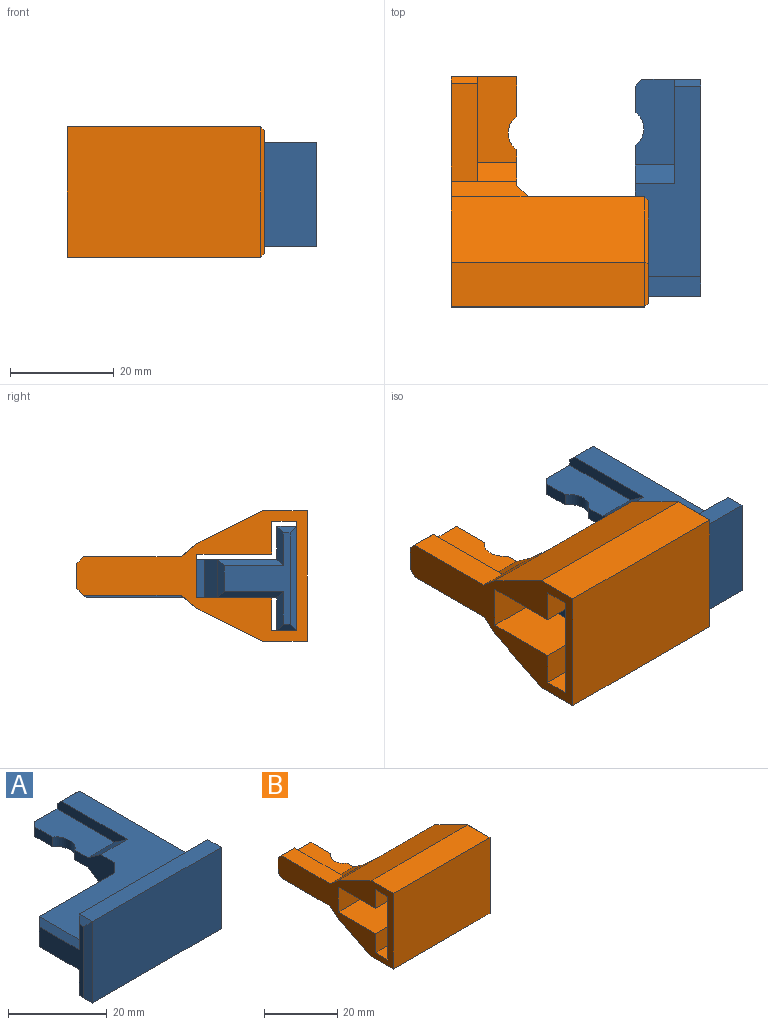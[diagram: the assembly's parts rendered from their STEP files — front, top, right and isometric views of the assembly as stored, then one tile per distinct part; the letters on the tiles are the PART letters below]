
ASSEMBLY  parts=2 mates=2
PART A: 32 faces, bbox 38.1x41.9x20.2 mm
  f0: plane 16.51x7.62mm, normal (0,0,1), area 117.4mm2, adj f2,f4,f6,f7,f8,f26,f29
  f1: plane 16.51x7.62mm, normal (0,0,-1), area 117.4mm2, adj f3,f4,f6,f7,f8,f26,f28
  f2: plane 7.62x3.63mm, normal (0,0.57,0.82), area 33.7mm2, adj f0,f4,f10,f29
  f3: plane 7.62x3.63mm, normal (0,0.57,-0.82), area 33.7mm2, adj f1,f4,f11,f28
  f4: plane 11.43x7.46mm, normal (-1,0,0), area 56.7mm2, adj f0,f1,f2,f3,f8,f10,f11,f27
  f5: plane 41.91x20.16mm, normal (1,0,0), area 359.5mm2, adj f6,f9,f10,f11,f12,f13,f14,f15
  f6: plane 11.43x4.92mm, normal (0,1,0), area 40.1mm2, adj f0,f1,f5,f26,f28,f29,f30,f31
  f7: plane 5.08x2.38mm, normal (-1,0,0), area 12.1mm2, adj f0,f1,f8,f26
  f8: cylinder r=3.81mm len=6.35mm, axis (0,0,-1), area 17.9mm2, adj f0,f1,f4,f7
  f9: plane 36.83x6.35mm, normal (0,1,0), area 233.9mm2, adj f5,f10,f15,f21
  f10: plane 36.83x36.83mm, normal (0,0,1), area 603mm2, adj f2,f4,f5,f9,f16,f23,f27,f29
  f11: plane 36.83x36.83mm, normal (0,0,-1), area 603mm2, adj f3,f4,f5,f12,f16,f24,f27,f28
  f12: plane 36.83x6.35mm, normal (0,1,0), area 233.9mm2, adj f5,f11,f13,f22
  f13: plane 36.83x3.81mm, normal (0,0,-1), area 140.3mm2, adj f5,f12,f14,f20
  f14: plane 36.83x20.16mm, normal (0,-1,0), area 742.5mm2, adj f5,f13,f15,f18
  f15: plane 36.83x3.81mm, normal (0,0,1), area 140.3mm2, adj f5,f9,f14,f19
  f16: plane 21.59x7.46mm, normal (0,1,0), area 161.1mm2, adj f10,f11,f25,f27
  f17: plane 17.62x12.7mm, normal (-1,0,0), area 78.6mm2, adj f18,f19,f20,f21,f22,f23,f24,f25
  f18: plane 20.16x1.27mm, normal (-0.71,-0.71,0), area 33.9mm2, adj f14,f17,f19,f20
  f19: plane 3.81x1.27mm, normal (-0.71,0,0.71), area 4.6mm2, adj f15,f17,f18,f21
  f20: plane 3.81x1.27mm, normal (-0.71,0,-0.71), area 4.6mm2, adj f13,f17,f18,f22
  f21: plane 7.62x1.27mm, normal (-0.71,0.71,0), area 11.4mm2, adj f9,f17,f19,f23
  f22: plane 7.62x1.27mm, normal (-0.71,0.71,0), area 11.4mm2, adj f12,f17,f20,f24
  f23: plane 12.7x1.27mm, normal (-0.71,0,0.71), area 20.5mm2, adj f10,f17,f21,f25
  f24: plane 12.7x1.27mm, normal (-0.71,0,-0.71), area 20.5mm2, adj f11,f17,f22,f25
  f25: plane 7.46x1.27mm, normal (-0.71,0.71,0), area 11.1mm2, adj f16,f17,f23,f24
  f26: plane 2.38x1.27mm, normal (-0.71,0.71,0), area 4.3mm2, adj f0,f1,f6,f7
  f27: plane 7.46x2.54mm, normal (-0.71,0.71,0), area 26.8mm2, adj f4,f10,f11,f16
  f28: plane 20.14x2.54mm, normal (-1,0,0), area 45.7mm2, adj f1,f3,f6,f11,f30
  f29: plane 20.14x2.54mm, normal (-1,0,0), area 45.7mm2, adj f0,f2,f6,f10,f31
  f30: plane 5.08x1.27mm, normal (0,0.71,-0.71), area 9.1mm2, adj f5,f6,f11,f28
  f31: plane 5.08x1.27mm, normal (0,0.71,0.71), area 9.1mm2, adj f5,f6,f10,f29
PART B: 49 faces, bbox 38.1x44.5x25.2 mm
  f0: plane 16.51x7.62mm, normal (0,0,1), area 118.2mm2, adj f3,f4,f5,f7,f8,f32
  f1: plane 16.51x7.62mm, normal (0,0,-1), area 118.2mm2, adj f2,f4,f5,f7,f8,f30
  f2: plane 7.62x3.63mm, normal (0,0.57,-0.82), area 33.7mm2, adj f1,f4,f26,f30
  f3: plane 7.62x3.63mm, normal (0,0.57,0.82), area 33.7mm2, adj f0,f4,f25,f32
  f4: plane 9.14x8.93mm, normal (1,0,0), area 49.3mm2, adj f0,f1,f2,f3,f7,f9,f10,f11
  f5: plane 12.7x4.92mm, normal (0,1,0), area 43.1mm2, adj f0,f1,f6,f8,f30,f32,f33,f34
  f6: plane 44.45x25.24mm, normal (-1,0,0), area 410.9mm2, adj f5,f9,f10,f11,f12,f13,f14,f15
  f7: cylinder r=3.81mm len=6.35mm, axis (0,0,-1), area 17.9mm2, adj f0,f1,f4,f8
  f8: plane 7.7x2.38mm, normal (1,0,0), area 18.3mm2, adj f0,f1,f5,f7
  f9: plane 12.7x8.48mm, normal (0,-1,0), area 107.7mm2, adj f4,f6,f10,f11
  f10: plane 37.34x16.58mm, normal (0,0,-1), area 540.5mm2, adj f4,f6,f9,f16,f24,f28,f35
  f11: plane 37.34x16.58mm, normal (0,0,1), area 540.5mm2, adj f4,f6,f9,f12,f23,f27,f47
  f12: plane 37.34x6.35mm, normal (0,-1,0), area 237.1mm2, adj f6,f11,f13,f45
  f13: plane 37.34x4.83mm, normal (0,0,1), area 180.2mm2, adj f6,f12,f14,f43
  f14: plane 37.34x21.18mm, normal (0,1,0), area 790.7mm2, adj f6,f13,f15,f41
  f15: plane 37.34x4.83mm, normal (0,0,-1), area 180.2mm2, adj f6,f14,f16,f39
  f16: plane 37.34x6.35mm, normal (0,-1,0), area 237.1mm2, adj f6,f10,f15,f37
  f17: plane 37.34x12.7mm, normal (0,0.45,-0.89), area 530.2mm2, adj f6,f18,f23,f26,f46
  f18: plane 37.34x8.57mm, normal (0,0,-1), area 320mm2, adj f6,f17,f19,f44
  f19: plane 37.34x25.24mm, normal (0,-1,0), area 942.5mm2, adj f6,f18,f20,f42
  f20: plane 37.34x8.57mm, normal (0,0,1), area 320mm2, adj f6,f19,f21,f40
  f21: plane 37.34x12.7mm, normal (0,0.45,0.89), area 530.2mm2, adj f6,f20,f24,f25,f38
  f22: plane 23.72x19.75mm, normal (1,0,0), area 121.8mm2, adj f35,f36,f37,f38,f39,f40,f41,f42
  f23: plane 22.47x2.03mm, normal (0,1,0), area 45.7mm2, adj f11,f17,f27,f48
  f24: plane 22.47x2.03mm, normal (0,1,0), area 45.7mm2, adj f10,f21,f28,f36
  f25: plane 14.86x3.04mm, normal (0,0.64,0.77), area 53.4mm2, adj f3,f4,f6,f21,f28,f31
  f26: plane 14.86x3.04mm, normal (0,0.64,-0.77), area 53.4mm2, adj f2,f4,f6,f17,f27,f29
  f27: plane 2.16x2.16mm, normal (0.71,0.71,0), area 3.5mm2, adj f4,f11,f23,f26
  f28: plane 2.16x2.16mm, normal (0.71,0.71,0), area 3.5mm2, adj f4,f10,f24,f25
  f29: plane 18.87x5.08mm, normal (0,0,-1), area 95.8mm2, adj f6,f26,f30,f34
  f30: plane 20.14x2.54mm, normal (1,0,0), area 45.7mm2, adj f1,f2,f5,f29,f34
  f31: plane 18.87x5.08mm, normal (0,0,1), area 95.8mm2, adj f6,f25,f32,f33
  f32: plane 20.14x2.54mm, normal (1,0,0), area 45.7mm2, adj f0,f3,f5,f31,f33
  f33: plane 5.08x1.27mm, normal (0,0.71,0.71), area 9.1mm2, adj f5,f6,f31,f32
  f34: plane 5.08x1.27mm, normal (0,0.71,-0.71), area 9.1mm2, adj f5,f6,f29,f30
  f35: plane 14.41x0.76mm, normal (0.71,0,-0.71), area 14.7mm2, adj f10,f22,f36,f37
  f36: plane 2.03x0.76mm, normal (0.71,0.71,0), area 1.5mm2, adj f22,f24,f35,f38
  f37: plane 7.11x0.76mm, normal (0.71,-0.71,0), area 6.8mm2, adj f16,f22,f35,f39
  f38: plane 12.88x6.82mm, normal (0.71,0.32,0.63), area 15mm2, adj f21,f22,f36,f40
  f39: plane 6.35x0.76mm, normal (0.71,0,-0.71), area 6mm2, adj f15,f22,f37,f41
  f40: plane 8.57x0.76mm, normal (0.71,0,0.71), area 8.7mm2, adj f20,f22,f38,f42
  f41: plane 22.7x0.76mm, normal (0.71,0.71,0), area 23.6mm2, adj f14,f22,f39,f43
  f42: plane 25.24x0.76mm, normal (0.71,-0.71,0), area 26.4mm2, adj f19,f22,f40,f44
  f43: plane 6.35x0.76mm, normal (0.71,0,0.71), area 6mm2, adj f13,f22,f41,f45
  f44: plane 8.57x0.76mm, normal (0.71,0,-0.71), area 8.7mm2, adj f18,f22,f42,f46
  f45: plane 7.11x0.76mm, normal (0.71,-0.71,0), area 6.8mm2, adj f12,f22,f43,f47
  f46: plane 12.88x6.82mm, normal (0.71,0.32,-0.63), area 15mm2, adj f17,f22,f44,f48
  f47: plane 14.41x0.76mm, normal (0.71,0,0.71), area 14.7mm2, adj f11,f22,f45,f48
  f48: plane 2.03x0.76mm, normal (0.71,0.71,0), area 1.5mm2, adj f22,f23,f46,f47
PLACE A t=(-28.78,-14.65,2.06)mm
PLACE B t=(0,-14.14,2.57)mm
MATE planar A.f13 <-> B.f13  axis (0,0,-1) through (-34.49,-41.95,-6.83)mm
MATE planar A.f14 <-> B.f14  axis (0,-1,0) through (-34.49,-43.86,3.25)mm
